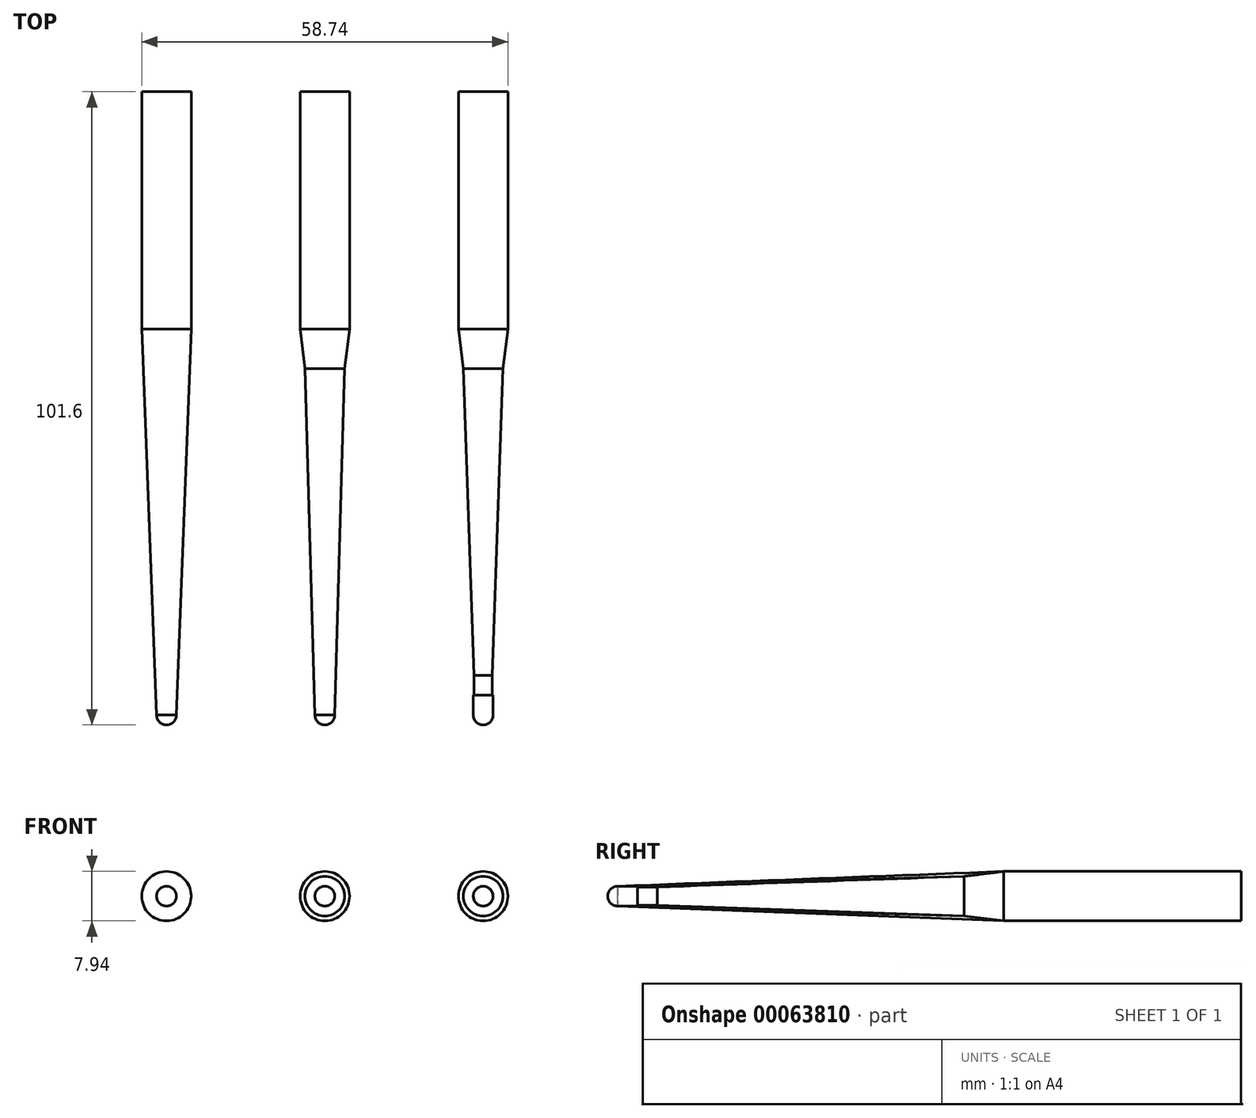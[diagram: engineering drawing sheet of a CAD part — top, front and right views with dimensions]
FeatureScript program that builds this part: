
annotation { "Feature Type Name" : "Feature", "Feature Type Description" : "" }
export const myFeature = defineFeature(function(context is Context, id is Id, definition is map)
    precondition{}
    {
        {
            var Q0;
            Q0=qCreatedBy(makeId("Top.planeOp"),FACE);
            var sketch = newSketch(context, id + "F0", { "sketchPlane" : qUnion([Q0])});
            skLineSegment(sketch, "E0", {"start": v(1.59, 4.76) * mm, "end": v(1.46, 4.76) * mm});
            skLineSegment(sketch, "E1", {"start": v(1.46, 4.76) * mm, "end": v(1.46, 7.94) * mm});
            skLineSegment(sketch, "E2", {"start": v(3.97, 63.5) * mm, "end": v(3.97, 101.6) * mm});
            skLineSegment(sketch, "E3", {"start": v(3.97, 101.6) * mm, "end": v(0, 101.6) * mm});
            skLineSegment(sketch, "E4", {"start": v(0, 101.6) * mm, "end": v(0, 0) * mm});
            skLineSegment(sketch, "E5", {"start": v(1.59, 4.76) * mm, "end": v(1.59, 1.59) * mm});
            skArc(sketch, "E6", {"start": v(0, 0) * mm, "mid": v(1.12, 0.46) * mm, "end": v(1.59, 1.59) * mm});
            skLineSegment(sketch, "E7", {"start": v(1.46, 7.94) * mm, "end": v(3.17, 57.15) * mm});
            skLineSegment(sketch, "E8", {"start": v(3.17, 57.15) * mm, "end": v(3.97, 63.5) * mm});
            skSolve(sketch);
        }
        {
            var Q0;
            Q0=makeQuery(id+"F0.imprint","IMPRINT",FACE,{"disambiguationData":[TD([[makeQuery(id+"F0.imprint","IMPRINT",EDGE,{"derivedFrom":sQuery(id+"F0.wireOp",EDGE,"E0")}),1.0]])]});
            var Q1;
            Q1=sQuery(id+"F0.wireOp",EDGE,"E4");
            revolve(context, id + "F1", {"surfaceOperationType" : NewSurfaceOperationType.NEW, "entities" : qUnion([Q0]), "axis" : qUnion([Q1]), "revolveType" : RevolveType.FULL});
        }
        {
            var Q0;
            Q0=makeQuery(id+"F1.opRevolve","SWEPT_BODY",BODY,{"disambiguationData":[OSD([sQuery(id+"F0.wireOp",EDGE,"E0"),sQuery(id+"F0.wireOp",EDGE,"E1"),sQuery(id+"F0.wireOp",EDGE,"E2"),sQuery(id+"F0.wireOp",EDGE,"E3"),sQuery(id+"F0.wireOp",EDGE,"E4"),sQuery(id+"F0.wireOp",EDGE,"E5"),sQuery(id+"F0.wireOp",EDGE,"E6"),sQuery(id+"F0.wireOp",EDGE,"E7"),sQuery(id+"F0.wireOp",EDGE,"E8")])]});
            transform(context, id + "F2", {"entities" : qUnion([Q0]), "transformType" : TransformType.TRANSLATION_3D, "dx" : 25.4 * mm, "dy" : 0 * mm, "dz" : 0 * mm, "makeCopy" : false});
        }
        {
            var Q0;
            Q0=makeQuery(id+"F0.imprint","IMPRINT",FACE,{"disambiguationData":[TD([[makeQuery(id+"F0.imprint","IMPRINT",EDGE,{"derivedFrom":sQuery(id+"F0.wireOp",EDGE,"E0")}),1.0]])]});
            var sketch = newSketch(context, id + "F3", { "sketchPlane" : qUnion([Q0])});
            skArc(sketch, "E9.0", {"start": v(0, 0) * mm, "mid": v(1.12, 0.46) * mm, "end": v(1.59, 1.59) * mm});
            skLineSegment(sketch, "E10", {"start": v(3.17, 57.15) * mm, "end": v(1.59, 1.59) * mm});
            skLineSegment(sketch, "E11", {"start": v(3.17, 57.15) * mm, "end": v(3.97, 63.5) * mm});
            skLineSegment(sketch, "E12", {"start": v(3.97, 63.5) * mm, "end": v(3.97, 101.6) * mm});
            skLineSegment(sketch, "E13", {"start": v(3.97, 101.6) * mm, "end": v(0, 101.6) * mm});
            skLineSegment(sketch, "E14", {"start": v(0, 101.6) * mm, "end": v(0, 0) * mm});
            skSolve(sketch);
        }
        {
            var Q0;
            Q0 = qSketchRegion(id + "F3", true);
            var Q1;
            Q1=sQuery(id+"F3.wireOp",EDGE,"E14");
            revolve(context, id + "F4", {"surfaceOperationType" : NewSurfaceOperationType.NEW, "entities" : qUnion([Q0]), "axis" : qUnion([Q1]), "revolveType" : RevolveType.FULL});
        }
        {
            var Q0;
            Q0=makeQuery(id+"F4.opRevolve","SWEPT_BODY",BODY,{"disambiguationData":[OSD([sQuery(id+"F3.wireOp",EDGE,"E9.0"),sQuery(id+"F3.wireOp",EDGE,"E10"),sQuery(id+"F3.wireOp",EDGE,"E11"),sQuery(id+"F3.wireOp",EDGE,"E12"),sQuery(id+"F3.wireOp",EDGE,"E13"),sQuery(id+"F3.wireOp",EDGE,"E14")])]});
            var Q1;
            Q1=makeQuery(id+"F1.opRevolve","SWEPT_BODY",BODY,{"disambiguationData":[OSD([sQuery(id+"F0.wireOp",EDGE,"E0"),sQuery(id+"F0.wireOp",EDGE,"E1"),sQuery(id+"F0.wireOp",EDGE,"E2"),sQuery(id+"F0.wireOp",EDGE,"E3"),sQuery(id+"F0.wireOp",EDGE,"E4"),sQuery(id+"F0.wireOp",EDGE,"E5"),sQuery(id+"F0.wireOp",EDGE,"E6"),sQuery(id+"F0.wireOp",EDGE,"E7"),sQuery(id+"F0.wireOp",EDGE,"E8")])]});
            transform(context, id + "F5", {"entities" : qUnion([Q0, Q1]), "transformType" : TransformType.TRANSLATION_3D, "dx" : 25.4 * mm, "dy" : 0 * mm, "dz" : 0 * mm, "makeCopy" : false});
        }
        {
            var Q0;
            Q0=makeQuery(id+"F0.imprint","IMPRINT",FACE,{"disambiguationData":[TD([[makeQuery(id+"F0.imprint","IMPRINT",EDGE,{"derivedFrom":sQuery(id+"F0.wireOp",EDGE,"E0")}),1.0]])]});
            var sketch = newSketch(context, id + "F6", { "sketchPlane" : qUnion([Q0])});
            skArc(sketch, "E15", {"start": v(0, 0) * mm, "mid": v(1.12, 0.46) * mm, "end": v(1.59, 1.59) * mm});
            skLineSegment(sketch, "E16", {"start": v(1.59, 1.59) * mm, "end": v(3.97, 63.5) * mm});
            skLineSegment(sketch, "E17", {"start": v(3.97, 63.5) * mm, "end": v(3.97, 101.6) * mm});
            skLineSegment(sketch, "E18", {"start": v(3.97, 101.6) * mm, "end": v(0, 101.6) * mm});
            skLineSegment(sketch, "E19", {"start": v(0, 101.6) * mm, "end": v(0, 0) * mm});
            skSolve(sketch);
        }
        {
            var Q0;
            Q0 = qSketchRegion(id + "F6", true);
            var Q1;
            Q1=sQuery(id+"F6.wireOp",EDGE,"E19");
            revolve(context, id + "F7", {"surfaceOperationType" : NewSurfaceOperationType.NEW, "entities" : qUnion([Q0]), "axis" : qUnion([Q1]), "revolveType" : RevolveType.FULL});
        }
        {
            var Q0;
            Q0=qCreatedBy(makeId("Top.planeOp"),FACE);
            var sketch = newSketch(context, id + "F8", { "sketchPlane" : qUnion([Q0])});
            skLineSegment(sketch, "E20", {"start": v(-1.59, 1.59) * mm, "end": v(-3.97, 63.5) * mm});
            skLineSegment(sketch, "E21", {"start": v(3.97, 63.5) * mm, "end": v(1.59, 1.59) * mm});
            skLineSegment(sketch, "E22", {"start": v(22.22, 57.15) * mm, "end": v(23.81, 1.59) * mm});
            skLineSegment(sketch, "E23", {"start": v(26.99, 1.59) * mm, "end": v(28.57, 57.15) * mm});
            skLineSegment(sketch, "E24", {"start": v(49.34, 7.94) * mm, "end": v(47.62, 57.15) * mm});
            skLineSegment(sketch, "E25", {"start": v(53.98, 57.15) * mm, "end": v(52.26, 7.94) * mm});
            skArc(sketch, "E26", {"start": v(26.99, 1.59) * mm, "mid": v(25.4, 0) * mm, "end": v(23.81, 1.59) * mm});
            skLineSegment(sketch, "E27", {"start": v(0, 0) * mm, "end": v(46.9, 0) * mm, "construction": true});
            skArc(sketch, "E28", {"start": v(1.59, 1.59) * mm, "mid": v(0, 0) * mm, "end": v(-1.59, 1.59) * mm});
            skLineSegment(sketch, "E29", {"start": v(49.34, 4.76) * mm, "end": v(49.34, 7.94) * mm});
            skLineSegment(sketch, "E30", {"start": v(52.26, 7.94) * mm, "end": v(52.26, 4.76) * mm});
            skLineSegment(sketch, "E31", {"start": v(49.21, 4.76) * mm, "end": v(49.21, 1.59) * mm});
            skLineSegment(sketch, "E32", {"start": v(52.39, 1.59) * mm, "end": v(52.39, 4.76) * mm});
            skArc(sketch, "E33", {"start": v(52.39, 1.59) * mm, "mid": v(50.8, 0) * mm, "end": v(49.21, 1.59) * mm});
            skLineSegment(sketch, "E34", {"start": v(0, 0) * mm, "end": v(0, 63.6) * mm, "construction": true});
            skLineSegment(sketch, "E35", {"start": v(25.4, 1.59) * mm, "end": v(25.4, 57.3) * mm, "construction": true});
            skLineSegment(sketch, "E36", {"start": v(50.8, 1.59) * mm, "end": v(50.8, 57.97) * mm, "construction": true});
            skLineSegment(sketch, "E37", {"start": v(22.22, 57.15) * mm, "end": v(21.43, 63.5) * mm});
            skLineSegment(sketch, "E38", {"start": v(29.37, 63.5) * mm, "end": v(28.57, 57.15) * mm});
            skLineSegment(sketch, "E39", {"start": v(21.43, 63.5) * mm, "end": v(21.43, 101.6) * mm});
            skLineSegment(sketch, "E40", {"start": v(29.37, 101.6) * mm, "end": v(29.37, 63.5) * mm});
            skLineSegment(sketch, "E41", {"start": v(47.62, 57.15) * mm, "end": v(46.83, 63.5) * mm});
            skLineSegment(sketch, "E42", {"start": v(54.77, 63.5) * mm, "end": v(53.97, 57.15) * mm});
            skLineSegment(sketch, "E43", {"start": v(46.83, 63.5) * mm, "end": v(46.83, 101.6) * mm});
            skLineSegment(sketch, "E44", {"start": v(54.77, 101.6) * mm, "end": v(54.77, 63.5) * mm});
            skLineSegment(sketch, "E45", {"start": v(-3.97, 63.5) * mm, "end": v(-3.97, 101.6) * mm});
            skLineSegment(sketch, "E46", {"start": v(3.97, 101.6) * mm, "end": v(3.97, 63.5) * mm});
            skSolve(sketch);
        }
    });
